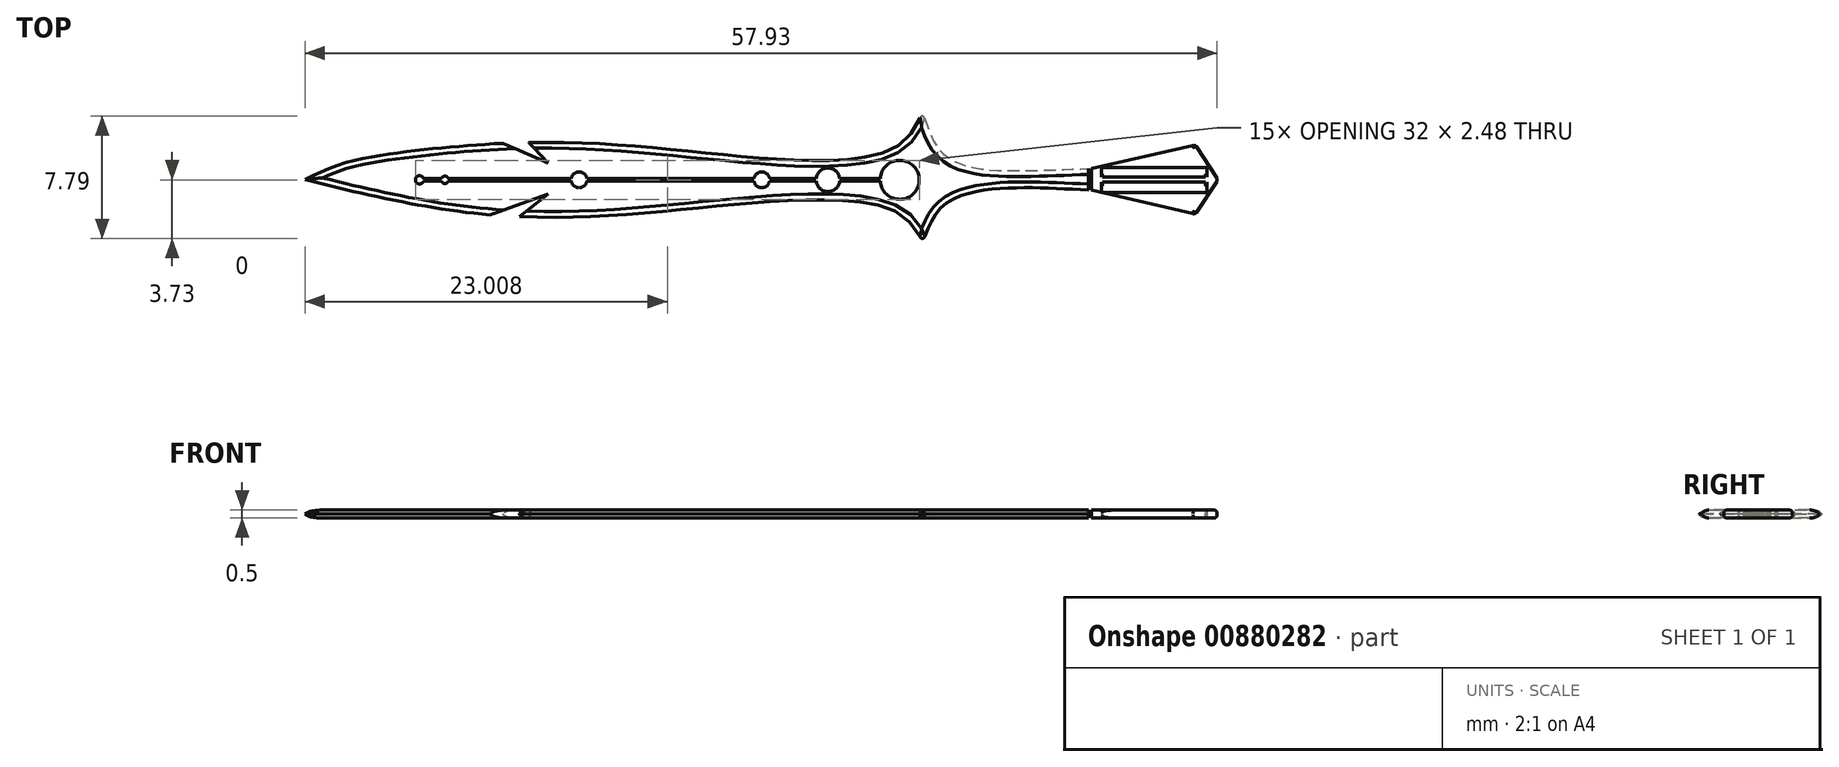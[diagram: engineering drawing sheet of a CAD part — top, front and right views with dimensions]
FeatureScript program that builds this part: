
annotation { "Feature Type Name" : "Feature", "Feature Type Description" : "" }
export const myFeature = defineFeature(function(context is Context, id is Id, definition is map)
    precondition{}
    {
        {
            var Q0;
            Q0=qCreatedBy(makeId("Top.planeOp"),FACE);
            var sketch = newSketch(context, id + "F0", { "sketchPlane" : qUnion([Q0])});
            skCircle(sketch, "E0", {"center": v(0, 0) * mm, "radius": 1.24 * mm});
            skCircle(sketch, "E1", {"center": v(-4.56, 0) * mm, "radius": 0.75 * mm});
            skCircle(sketch, "E2", {"center": v(-8.76, 0) * mm, "radius": 0.5 * mm});
            skCircle(sketch, "E3", {"center": v(-20.37, 0) * mm, "radius": 0.5 * mm});
            skCircle(sketch, "E4", {"center": v(-28.89, 0) * mm, "radius": 0.23 * mm});
            skCircle(sketch, "E5", {"center": v(-30.5, 0) * mm, "radius": 0.26 * mm});
            skFitSpline(sketch, "E6", {"points": [v(-37.86, 0) * mm, v(-29.65, -1.8) * mm, v(-17.5, -2.24) * mm, v(0, -2.2) * mm, v(1.46, -3.8) * mm, v(2.62, -1.8) * mm, v(12, -0.68) * mm], "startDerivative": vector(46.4, -11.45) * mm, "endDerivative": vector(63.67, -3.45) * mm});
            skFitSpline(sketch, "E7", {"points": [v(-37.86, 0) * mm, v(-35.22, 1.1) * mm, v(-29.65, 2) * mm, v(-17.5, 2.22) * mm, v(0, 2.27) * mm, v(1.46, 4.14) * mm, v(2.62, 1.82) * mm, v(8.07, 0.62) * mm, v(12, 0.75) * mm], "startDerivative": vector(27.22, 13.68) * mm, "endDerivative": vector(34.2, 1.53) * mm});
            skLineSegment(sketch, "E8", {"start": v(12, -0.68) * mm, "end": v(12, 0.75) * mm});
            skSolve(sketch);
        }
        {
            var Q0;
            Q0=makeQuery(id+"F0.imprint","IMPRINT",FACE,{"disambiguationData":[TD([[makeQuery(id+"F0.imprint","IMPRINT",EDGE,{"derivedFrom":sQuery(id+"F0.wireOp",EDGE,"E0")}),-1.0]])]});
            var Q1;
            Q1=sQuery(id+"F0.wireOp",EDGE,"E3");
            var Q2;
            Q2=sQuery(id+"F0.wireOp",EDGE,"E7");
            var Q3;
            Q3=sQuery(id+"F0.wireOp",EDGE,"E2");
            var Q4;
            Q4=sQuery(id+"F0.wireOp",EDGE,"E6");
            var Q5;
            Q5=sQuery(id+"F0.wireOp",EDGE,"E0");
            var Q6;
            Q6=sQuery(id+"F0.wireOp",EDGE,"E1");
            var Q7;
            Q7=sQuery(id+"F0.wireOp",EDGE,"E5");
            var Q8;
            Q8=sQuery(id+"F0.wireOp",EDGE,"E4");
            var Q9;
            Q9=sQuery(id+"F0.wireOp",EDGE,"E8");
            extrude(context, id + "F1", {"entities" : qUnion([Q0]), "surfaceEntities" : qUnion([Q1, Q2, Q3, Q4, Q5, Q6, Q7, Q8, Q9]), "depth" : .5 * mm, "offsetDistance" : 25 * mm});
        }
        {
            var Q0;
            Q0=makeQuery(id+"F1.opExtrude","CAP_EDGE",EDGE,{"disambiguationData":[OSD([sQuery(id+"F0.wireOp",EDGE,"E6")])],"isStart":false});
            var Q1;
            Q1=makeQuery(id+"F1.opExtrude","CAP_EDGE",EDGE,{"disambiguationData":[OSD([sQuery(id+"F0.wireOp",EDGE,"E7")])],"isStart":false});
            var Q2;
            Q2=makeQuery(id+"F1.opExtrude","CAP_EDGE",EDGE,{"disambiguationData":[OSD([sQuery(id+"F0.wireOp",EDGE,"E7")])],"isStart":true});
            var Q3;
            Q3=makeQuery(id+"F1.opExtrude","CAP_EDGE",EDGE,{"disambiguationData":[OSD([sQuery(id+"F0.wireOp",EDGE,"E6")])],"isStart":true});
            fillet(context, id + "F2", {"entities" : qUnion([Q0, Q1, Q2, Q3]), "radius" : .4 * mm, "tangentPropagation" : true, "allowEdgeOverflow" : false});
        }
        {
            var Q0;
            Q0=qCreatedBy(makeId("Top.planeOp"),FACE);
            var sketch = newSketch(context, id + "F3", { "sketchPlane" : qUnion([Q0])});
            skLineSegment(sketch, "E9.bottom", {"start": v(-30.76, 0) * mm, "end": v(1.24, 0) * mm});
            skLineSegment(sketch, "E9.top", {"start": v(-30.76, 0) * mm, "end": v(1.24, 0) * mm});
            skLineSegment(sketch, "E9.left", {"start": v(-30.76, 0) * mm, "end": v(-30.76, 0) * mm});
            skLineSegment(sketch, "E9.right", {"start": v(1.24, 0) * mm, "end": v(1.24, 0) * mm});
            skSolve(sketch);
        }
        {
            var Q0;
            Q0=makeQuery(id+"F3.imprint","IMPRINT",FACE,{"disambiguationData":[TD([[makeQuery(id+"F3.imprint","IMPRINT",EDGE,{"derivedFrom":sQuery(id+"F3.wireOp",EDGE,"E9.bottom")}),1.0]])]});
            extrude(context, id + "F4", {"entities" : qUnion([Q0]), "operationType" : NewBodyOperationType.REMOVE, "depth" : 25 * mm, "offsetDistance" : 25 * mm});
        }
        {
            var Q0;
            Q0=qCreatedBy(makeId("Top.planeOp"),FACE);
            var sketch = newSketch(context, id + "F5", { "sketchPlane" : qUnion([Q0])});
            skLineSegment(sketch, "E10", {"start": v(-28.33, -3.05) * mm, "end": v(-22.32, -0.92) * mm});
            skLineSegment(sketch, "E11", {"start": v(-22.32, -0.92) * mm, "end": v(-26.34, -4.04) * mm});
            skLineSegment(sketch, "E12", {"start": v(-26.34, -4.04) * mm, "end": v(-28.33, -3.05) * mm});
            skLineSegment(sketch, "E13", {"start": v(-28.33, 3.67) * mm, "end": v(-22.32, 1.07) * mm});
            skLineSegment(sketch, "E14", {"start": v(-22.32, 1.07) * mm, "end": v(-26.34, 5.28) * mm});
            skLineSegment(sketch, "E15", {"start": v(-26.34, 5.28) * mm, "end": v(-28.33, 3.67) * mm});
            skSolve(sketch);
        }
        {
            var Q0;
            Q0=makeQuery(id+"F5.imprint","IMPRINT",FACE,{"disambiguationData":[TD([[makeQuery(id+"F5.imprint","IMPRINT",EDGE,{"derivedFrom":sQuery(id+"F5.wireOp",EDGE,"E13")}),1.0]])]});
            var Q1;
            Q1=makeQuery(id+"F5.imprint","IMPRINT",FACE,{"disambiguationData":[TD([[makeQuery(id+"F5.imprint","IMPRINT",EDGE,{"derivedFrom":sQuery(id+"F5.wireOp",EDGE,"E10")}),-1.0]])]});
            extrude(context, id + "F6", {"entities" : qUnion([Q0, Q1]), "operationType" : NewBodyOperationType.REMOVE, "depth" : 25 * mm, "offsetDistance" : 25 * mm});
        }
        {
            var Q0;
            Q0=qCreatedBy(makeId("Top.planeOp"),FACE);
            var sketch = newSketch(context, id + "F7", { "sketchPlane" : qUnion([Q0])});
            skLineSegment(sketch, "E16.bottom", {"start": v(-30.76, 0) * mm, "end": v(-0.08, 0) * mm});
            skLineSegment(sketch, "E16.top", {"start": v(-30.76, 0) * mm, "end": v(-0.08, 0) * mm});
            skLineSegment(sketch, "E16.left", {"start": v(-30.76, 0) * mm, "end": v(-30.76, 0) * mm});
            skLineSegment(sketch, "E16.right", {"start": v(-0.08, 0) * mm, "end": v(-0.08, 0) * mm});
            skSolve(sketch);
        }
        {
            var Q0;
            Q0=makeQuery(id+"F7.imprint","IMPRINT",FACE,{"disambiguationData":[TD([[makeQuery(id+"F7.imprint","IMPRINT",EDGE,{"derivedFrom":sQuery(id+"F7.wireOp",EDGE,"E16.bottom")}),1.0]])]});
            extrude(context, id + "F8", {"entities" : qUnion([Q0]), "operationType" : NewBodyOperationType.REMOVE, "depth" : 25 * mm, "offsetDistance" : 25 * mm});
        }
        {
            var Q0;
            Q0=qCreatedBy(makeId("Top.planeOp"),FACE);
            var sketch = newSketch(context, id + "F9", { "sketchPlane" : qUnion([Q0])});
            skLineSegment(sketch, "E17.bottom", {"start": v(-0.13, -0.07) * mm, "end": v(-30.5, -0.07) * mm});
            skLineSegment(sketch, "E17.top", {"start": v(-0.13, 0.09) * mm, "end": v(-30.5, 0.09) * mm});
            skLineSegment(sketch, "E17.left", {"start": v(-0.13, -0.07) * mm, "end": v(-0.13, 0.09) * mm});
            skLineSegment(sketch, "E17.right", {"start": v(-30.5, -0.07) * mm, "end": v(-30.5, 0.09) * mm});
            skSolve(sketch);
        }
        {
            var Q0;
            Q0=makeQuery(id+"F9.imprint","IMPRINT",FACE,{"disambiguationData":[TD([[makeQuery(id+"F9.imprint","IMPRINT",EDGE,{"derivedFrom":sQuery(id+"F9.wireOp",EDGE,"E17.bottom")}),-1.0]])]});
            extrude(context, id + "F10", {"entities" : qUnion([Q0]), "operationType" : NewBodyOperationType.REMOVE, "depth" : 25 * mm, "offsetDistance" : 25 * mm});
        }
        {
            var Q0;
            Q0=qCreatedBy(makeId("Top.planeOp"),FACE);
            var sketch = newSketch(context, id + "F11", { "sketchPlane" : qUnion([Q0])});
            skLineSegment(sketch, "E18", {"start": v(12.18, 0.72) * mm, "end": v(18.78, 2.22) * mm});
            skLineSegment(sketch, "E19", {"start": v(18.78, 2.22) * mm, "end": v(20.2, 0) * mm});
            skLineSegment(sketch, "E20", {"start": v(20.2, 0) * mm, "end": v(18.78, -2.19) * mm});
            skLineSegment(sketch, "E21", {"start": v(18.78, -2.19) * mm, "end": v(12.18, -0.66) * mm});
            skLineSegment(sketch, "E22", {"start": v(12.18, -0.66) * mm, "end": v(12.18, 0.72) * mm});
            skSolve(sketch);
        }
        {
            var Q0;
            Q0=makeQuery(id+"F11.imprint","IMPRINT",FACE,{"disambiguationData":[TD([[makeQuery(id+"F11.imprint","IMPRINT",EDGE,{"derivedFrom":sQuery(id+"F11.wireOp",EDGE,"E18")}),-1.0]])]});
            extrude(context, id + "F12", {"entities" : qUnion([Q0]), "operationType" : NewBodyOperationType.ADD, "depth" : .5 * mm, "offsetDistance" : 25 * mm});
        }
        {
            var Q0;
            Q0=qCreatedBy(makeId("Top.planeOp"),FACE);
            var sketch = newSketch(context, id + "F13", { "sketchPlane" : qUnion([Q0])});
            skLineSegment(sketch, "E23.bottom", {"start": v(12.81, 0.38) * mm, "end": v(19.52, 0.38) * mm});
            skLineSegment(sketch, "E23.top", {"start": v(12.81, 0.8) * mm, "end": v(19.52, 0.8) * mm});
            skLineSegment(sketch, "E23.left", {"start": v(12.81, 0.38) * mm, "end": v(12.81, 0.8) * mm});
            skLineSegment(sketch, "E23.right", {"start": v(19.52, 0.38) * mm, "end": v(19.52, 0.8) * mm});
            skLineSegment(sketch, "E24.bottom", {"start": v(19.52, -0.34) * mm, "end": v(12.82, -0.34) * mm});
            skLineSegment(sketch, "E24.top", {"start": v(19.52, -0.8) * mm, "end": v(12.82, -0.8) * mm});
            skLineSegment(sketch, "E24.left", {"start": v(19.52, -0.34) * mm, "end": v(19.52, -0.8) * mm});
            skLineSegment(sketch, "E24.right", {"start": v(12.82, -0.34) * mm, "end": v(12.82, -0.8) * mm});
            skSolve(sketch);
        }
        {
            var Q0;
            Q0=makeQuery(id+"F13.imprint","IMPRINT",FACE,{"disambiguationData":[TD([[makeQuery(id+"F13.imprint","IMPRINT",EDGE,{"derivedFrom":sQuery(id+"F13.wireOp",EDGE,"E24.bottom")}),1.0]])]});
            var Q1;
            Q1=makeQuery(id+"F13.imprint","IMPRINT",FACE,{"disambiguationData":[TD([[makeQuery(id+"F13.imprint","IMPRINT",EDGE,{"derivedFrom":sQuery(id+"F13.wireOp",EDGE,"E23.bottom")}),1.0]])]});
            extrude(context, id + "F14", {"entities" : qUnion([Q0, Q1]), "operationType" : NewBodyOperationType.REMOVE, "depth" : 25 * mm, "offsetDistance" : 25 * mm});
        }
        {
            var Q0;
            Q0=makeQuery(id+"F14.boolean.opBoolean","COPY",EDGE,{"derivedFrom":makeQuery(id+"F14.opExtrude","CAP_EDGE",EDGE,{"disambiguationData":[OSD([sQuery(id+"F13.wireOp",EDGE,"E23.bottom")])],"isStart":true})});
            var Q1;
            Q1=makeQuery(id+"F14.boolean.opBoolean","INTERSECT",EDGE,{"derivedFrom":[makeQuery(id+"F12.boolean.opBoolean","MERGE",FACE,{"derivedFrom":[makeQuery(id+"F1.opExtrude","CAP_FACE",FACE,{"disambiguationData":[OSD([sQuery(id+"F0.wireOp",EDGE,"E0"),sQuery(id+"F0.wireOp",EDGE,"E1"),sQuery(id+"F0.wireOp",EDGE,"E2"),sQuery(id+"F0.wireOp",EDGE,"E3"),sQuery(id+"F0.wireOp",EDGE,"E4"),sQuery(id+"F0.wireOp",EDGE,"E5"),sQuery(id+"F0.wireOp",EDGE,"E6"),sQuery(id+"F0.wireOp",EDGE,"E7"),sQuery(id+"F0.wireOp",EDGE,"E8")])],"isStart":false}),makeQuery(id+"F12.opExtrude","CAP_FACE",FACE,{"disambiguationData":[OSD([sQuery(id+"F11.wireOp",EDGE,"E18"),sQuery(id+"F11.wireOp",EDGE,"E19"),sQuery(id+"F11.wireOp",EDGE,"E20"),sQuery(id+"F11.wireOp",EDGE,"E21"),sQuery(id+"F11.wireOp",EDGE,"E22")])],"isStart":false})]}),makeQuery(id+"F14.opExtrude","SWEPT_FACE",FACE,{"disambiguationData":[OSD([sQuery(id+"F13.wireOp",EDGE,"E23.bottom")])]})]});
            var Q2;
            Q2=makeQuery(id+"F14.boolean.opBoolean","COPY",EDGE,{"derivedFrom":makeQuery(id+"F14.opExtrude","CAP_EDGE",EDGE,{"disambiguationData":[OSD([sQuery(id+"F13.wireOp",EDGE,"E24.bottom")])],"isStart":true})});
            var Q3;
            Q3=makeQuery(id+"F14.boolean.opBoolean","INTERSECT",EDGE,{"derivedFrom":[makeQuery(id+"F12.boolean.opBoolean","MERGE",FACE,{"derivedFrom":[makeQuery(id+"F1.opExtrude","CAP_FACE",FACE,{"disambiguationData":[OSD([sQuery(id+"F0.wireOp",EDGE,"E0"),sQuery(id+"F0.wireOp",EDGE,"E1"),sQuery(id+"F0.wireOp",EDGE,"E2"),sQuery(id+"F0.wireOp",EDGE,"E3"),sQuery(id+"F0.wireOp",EDGE,"E4"),sQuery(id+"F0.wireOp",EDGE,"E5"),sQuery(id+"F0.wireOp",EDGE,"E6"),sQuery(id+"F0.wireOp",EDGE,"E7"),sQuery(id+"F0.wireOp",EDGE,"E8")])],"isStart":false}),makeQuery(id+"F12.opExtrude","CAP_FACE",FACE,{"disambiguationData":[OSD([sQuery(id+"F11.wireOp",EDGE,"E18"),sQuery(id+"F11.wireOp",EDGE,"E19"),sQuery(id+"F11.wireOp",EDGE,"E20"),sQuery(id+"F11.wireOp",EDGE,"E21"),sQuery(id+"F11.wireOp",EDGE,"E22")])],"isStart":false})]}),makeQuery(id+"F14.opExtrude","SWEPT_FACE",FACE,{"disambiguationData":[OSD([sQuery(id+"F13.wireOp",EDGE,"E24.bottom")])]})]});
            var Q4;
            Q4=makeQuery(id+"F12.opExtrude","CAP_EDGE",EDGE,{"disambiguationData":[OSD([sQuery(id+"F11.wireOp",EDGE,"E18")])],"isStart":false});
            var Q5;
            Q5=makeQuery(id+"F12.opExtrude","CAP_EDGE",EDGE,{"disambiguationData":[OSD([sQuery(id+"F11.wireOp",EDGE,"E18")])],"isStart":true});
            var Q6;
            Q6=makeQuery(id+"F12.opExtrude","CAP_EDGE",EDGE,{"disambiguationData":[OSD([sQuery(id+"F11.wireOp",EDGE,"E21")])],"isStart":false});
            var Q7;
            Q7=makeQuery(id+"F12.opExtrude","CAP_EDGE",EDGE,{"disambiguationData":[OSD([sQuery(id+"F11.wireOp",EDGE,"E21")])],"isStart":true});
            fillet(context, id + "F15", {"entities" : qUnion([Q0, Q1, Q2, Q3, Q4, Q5, Q6, Q7]), "radius" : .2 * mm, "tangentPropagation" : true, "allowEdgeOverflow" : false});
        }
        {
            var Q0;
            Q0=makeQuery(id+"F12.opExtrude","SWEPT_FACE",FACE,{"disambiguationData":[OSD([sQuery(id+"F11.wireOp",EDGE,"E20")])]});
            var Q1;
            Q1=makeQuery(id+"F12.opExtrude","SWEPT_FACE",FACE,{"disambiguationData":[OSD([sQuery(id+"F11.wireOp",EDGE,"E19")])]});
            fillet(context, id + "F16", {"entities" : qUnion([Q0, Q1]), "radius" : .2 * mm, "tangentPropagation" : true, "allowEdgeOverflow" : false});
        }
        {
            var Q0;
            Q0=qCreatedBy(makeId("Top.planeOp"),FACE);
            var sketch = newSketch(context, id + "F17", { "sketchPlane" : qUnion([Q0])});
            skLineSegment(sketch, "E25.bottom", {"start": v(12.9, -0.13) * mm, "end": v(19.41, -0.13) * mm});
            skLineSegment(sketch, "E25.top", {"start": v(12.9, -0.57) * mm, "end": v(19.41, -0.57) * mm});
            skLineSegment(sketch, "E25.left", {"start": v(12.9, -0.13) * mm, "end": v(12.9, -0.57) * mm});
            skLineSegment(sketch, "E25.right", {"start": v(19.41, -0.13) * mm, "end": v(19.41, -0.57) * mm});
            skLineSegment(sketch, "E26.bottom", {"start": v(12.9, 0.18) * mm, "end": v(19.41, 0.18) * mm});
            skLineSegment(sketch, "E26.top", {"start": v(12.9, 0.58) * mm, "end": v(19.41, 0.58) * mm});
            skLineSegment(sketch, "E26.left", {"start": v(12.9, 0.18) * mm, "end": v(12.9, 0.58) * mm});
            skLineSegment(sketch, "E26.right", {"start": v(19.41, 0.18) * mm, "end": v(19.41, 0.58) * mm});
            skSolve(sketch);
        }
        {
            var Q0;
            Q0=makeQuery(id+"F17.imprint","IMPRINT",FACE,{"disambiguationData":[TD([[makeQuery(id+"F17.imprint","IMPRINT",EDGE,{"derivedFrom":sQuery(id+"F17.wireOp",EDGE,"E25.bottom")}),-1.0]])]});
            var Q1;
            Q1=makeQuery(id+"F17.imprint","IMPRINT",FACE,{"disambiguationData":[TD([[makeQuery(id+"F17.imprint","IMPRINT",EDGE,{"derivedFrom":sQuery(id+"F17.wireOp",EDGE,"E26.bottom")}),1.0]])]});
            extrude(context, id + "F18", {"entities" : qUnion([Q0, Q1]), "operationType" : NewBodyOperationType.REMOVE, "depth" : 25 * mm, "offsetDistance" : 25 * mm});
        }
    });
